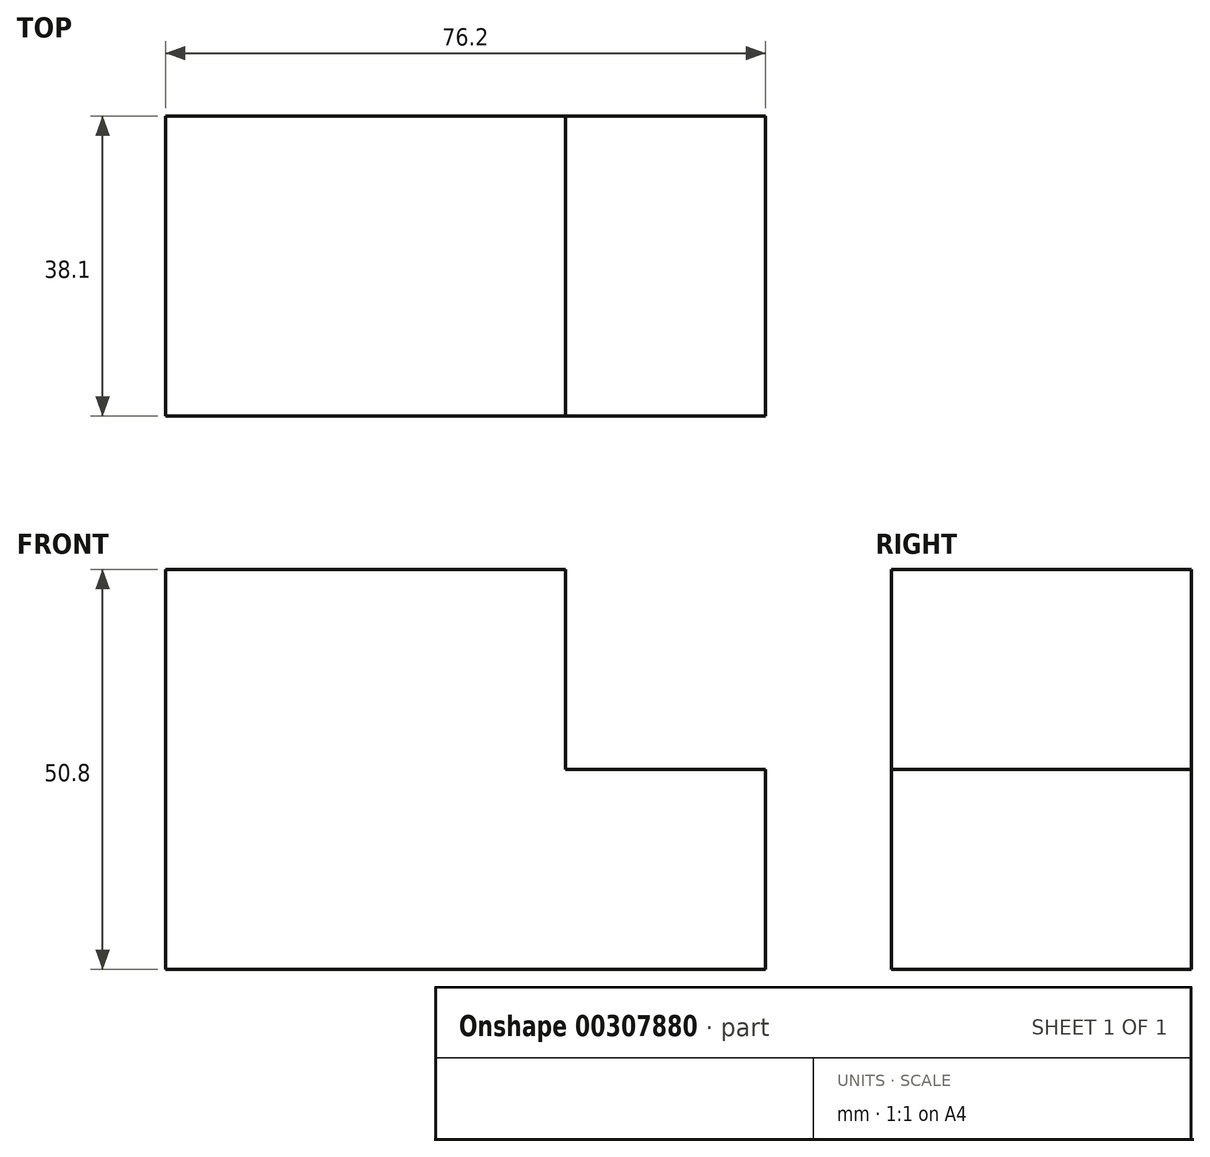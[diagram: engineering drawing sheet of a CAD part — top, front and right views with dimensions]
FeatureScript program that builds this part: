
annotation { "Feature Type Name" : "Feature", "Feature Type Description" : "" }
export const myFeature = defineFeature(function(context is Context, id is Id, definition is map)
    precondition{}
    {
        {
            var Q0;
            Q0=qCreatedBy(makeId("Front.planeOp"),FACE);
            var sketch = newSketch(context, id + "F0", { "sketchPlane" : qUnion([Q0])});
            skLineSegment(sketch, "E0", {"start": v(-38.87, -34.25) * mm, "end": v(37.33, -34.25) * mm});
            skLineSegment(sketch, "E1", {"start": v(37.33, -34.25) * mm, "end": v(37.33, -8.85) * mm});
            skLineSegment(sketch, "E2", {"start": v(37.33, -8.85) * mm, "end": v(11.93, -8.85) * mm});
            skLineSegment(sketch, "E3", {"start": v(11.93, -8.85) * mm, "end": v(11.93, 16.55) * mm});
            skLineSegment(sketch, "E4", {"start": v(11.93, 16.55) * mm, "end": v(-38.87, 16.55) * mm});
            skLineSegment(sketch, "E5", {"start": v(-38.87, 16.55) * mm, "end": v(-38.87, -34.25) * mm});
            skSolve(sketch);
        }
        {
            var Q0;
            Q0=makeQuery(id+"F0.imprint","IMPRINT",FACE,{"disambiguationData":[TD([[makeQuery(id+"F0.imprint","IMPRINT",EDGE,{"derivedFrom":sQuery(id+"F0.wireOp",EDGE,"E0")}),1.0]])]});
            extrude(context, id + "F1", {"entities" : qUnion([Q0]), "depth" : 38.1 * mm});
        }
    });
